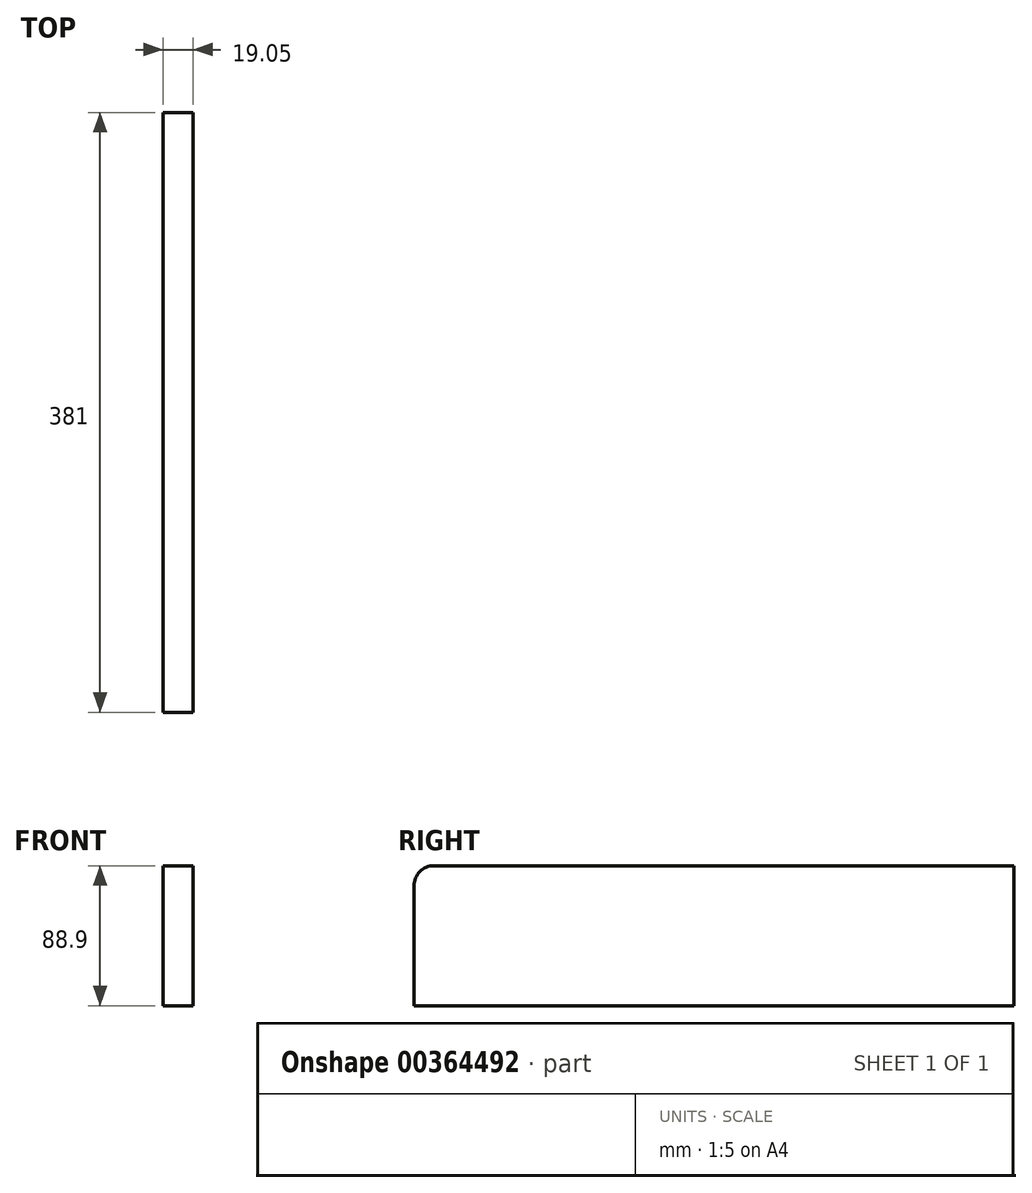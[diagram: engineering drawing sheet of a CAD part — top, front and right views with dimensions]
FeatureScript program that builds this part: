
annotation { "Feature Type Name" : "Feature", "Feature Type Description" : "" }
export const myFeature = defineFeature(function(context is Context, id is Id, definition is map)
    precondition{}
    {
        {
            var Q0;
            Q0=qCreatedBy(makeId("Right.planeOp"),FACE);
            var sketch = newSketch(context, id + "F0", { "sketchPlane" : qUnion([Q0])});
            skLineSegment(sketch, "E0.bottom", {"start": v(0, 0) * mm, "end": v(381, 0) * mm});
            skLineSegment(sketch, "E0.top", {"start": v(12.7, 88.9) * mm, "end": v(381, 88.9) * mm});
            skLineSegment(sketch, "E0.left", {"start": v(0, 0) * mm, "end": v(0, 76.2) * mm});
            skLineSegment(sketch, "E0.right", {"start": v(381, 0) * mm, "end": v(381, 88.9) * mm});
            skPoint(sketch, "E1.visualSharp", {"position": v(0, 88.9) * mm});
            skArc(sketch, "E1.filletArc", {"start": v(12.7, 88.9) * mm, "mid": v(3.72, 85.18) * mm, "end": v(0, 76.2) * mm});
            skSolve(sketch);
        }
        {
            var Q0;
            Q0=makeQuery(id+"F0.imprint","IMPRINT",FACE,{"disambiguationData":[TD([[makeQuery(id+"F0.imprint","IMPRINT",EDGE,{"derivedFrom":sQuery(id+"F0.wireOp",EDGE,"E0.bottom")}),1.0]])]});
            extrude(context, id + "F1", {"entities" : qUnion([Q0]), "depth" : 19.05 * mm});
        }
    });
